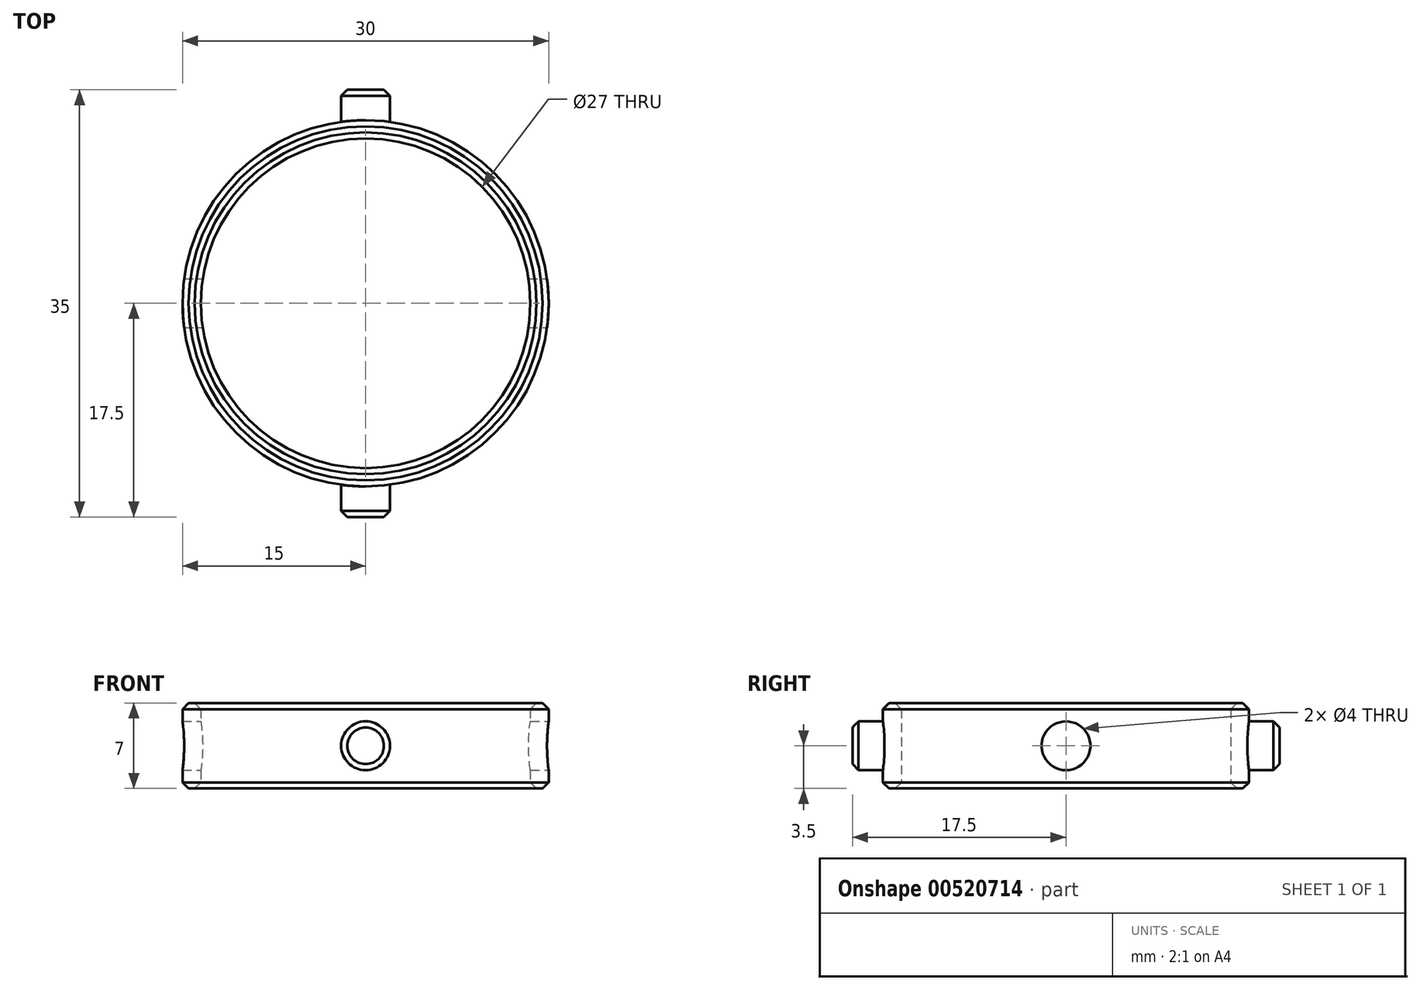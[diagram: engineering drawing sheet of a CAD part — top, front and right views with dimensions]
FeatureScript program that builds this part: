
annotation { "Feature Type Name" : "Feature", "Feature Type Description" : "" }
export const myFeature = defineFeature(function(context is Context, id is Id, definition is map)
    precondition{}
    {
        {
            var Q0;
            Q0=qCreatedBy(makeId("Top.planeOp"),FACE);
            var sketch = newSketch(context, id + "F0", { "sketchPlane" : qUnion([Q0])});
            skCircle(sketch, "E0", {"center": v(0, 0) * mm, "radius": 15 * mm});
            skCircle(sketch, "E1", {"center": v(0, 0) * mm, "radius": 13.5 * mm});
            skSolve(sketch);
        }
        {
            var Q0;
            Q0=makeQuery(id+"F0.imprint","IMPRINT",FACE,{"disambiguationData":[TD([[makeQuery(id+"F0.imprint","IMPRINT",EDGE,{"derivedFrom":sQuery(id+"F0.wireOp",EDGE,"E0")}),1.0]])]});
            extrude(context, id + "F1", {"entities" : qUnion([Q0]), "depth" : 7 * mm});
        }
        {
            var Q0;
            Q0=qCreatedBy(makeId("Right.planeOp"),FACE);
            var sketch = newSketch(context, id + "F2", { "sketchPlane" : qUnion([Q0])});
            skCircle(sketch, "E2", {"center": v(0, 3.5) * mm, "radius": 2 * mm});
            skLineSegment(sketch, "E3", {"start": v(0, 0) * mm, "end": v(0, 3.5) * mm, "construction": true});
            skLineSegment(sketch, "E4", {"start": v(0, 3.5) * mm, "end": v(0, 7) * mm, "construction": true});
            skSolve(sketch);
        }
        {
            var Q0;
            Q0=makeQuery(id+"F2.imprint","IMPRINT",FACE,{"disambiguationData":[TD([[makeQuery(id+"F2.imprint","IMPRINT",EDGE,{"derivedFrom":sQuery(id+"F2.wireOp",EDGE,"E2")}),1.0]])]});
            extrude(context, id + "F3", {"entities" : qUnion([Q0]), "operationType" : NewBodyOperationType.REMOVE, "endBound" : BoundingType.SYMMETRIC, "oppositeDirection" : true, "depth" : 40 * mm});
        }
        {
            var Q0;
            Q0=makeQuery(id+"F1.opExtrude","CAP_EDGE",EDGE,{"disambiguationData":[OSD([sQuery(id+"F0.wireOp",EDGE,"E0")])],"isStart":false});
            var Q1;
            Q1=makeQuery(id+"F1.opExtrude","CAP_EDGE",EDGE,{"disambiguationData":[OSD([sQuery(id+"F0.wireOp",EDGE,"E1")])],"isStart":false});
            var Q2;
            Q2=makeQuery(id+"F1.opExtrude","CAP_EDGE",EDGE,{"disambiguationData":[OSD([sQuery(id+"F0.wireOp",EDGE,"E0")])],"isStart":true});
            var Q3;
            Q3=makeQuery(id+"F1.opExtrude","CAP_EDGE",EDGE,{"disambiguationData":[OSD([sQuery(id+"F0.wireOp",EDGE,"E1")])],"isStart":true});
            chamfer(context, id + "F4", {"entities" : qUnion([Q0, Q1, Q2, Q3]), "width" : .5 * mm, "tangentPropagation" : true});
        }
        {
            var Q0;
            Q0=qCreatedBy(makeId("Front.planeOp"),FACE);
            cPlane(context, id + "F5", {"entities" : qUnion([Q0]), "cplaneType" : CPlaneType.OFFSET, "offset" : (27 / 2) * mm, "oppositeDirection" : true, "width" : 150 * mm, "height" : 150 * mm});
        }
        {
            var Q0;
            Q0=qCreatedBy(id+"F5.planeOp",FACE);
            var sketch = newSketch(context, id + "F6", { "sketchPlane" : qUnion([Q0])});
            skCircle(sketch, "E5", {"center": v(0, 3.5) * mm, "radius": 2 * mm});
            skLineSegment(sketch, "E6", {"start": v(0, 0) * mm, "end": v(0, 3.5) * mm, "construction": true});
            skLineSegment(sketch, "E7", {"start": v(0, 3.5) * mm, "end": v(0, 7) * mm, "construction": true});
            skSolve(sketch);
        }
        {
            var Q0;
            Q0=qSketchRegion(id+"F6",true);
            extrude(context, id + "F7", {"entities" : qUnion([Q0]), "operationType" : NewBodyOperationType.ADD, "oppositeDirection" : true, "depth" : 4 * mm});
        }
        {
            var Q0;
            Q0=makeQuery(id+"F1.opExtrude","SWEPT_BODY",BODY,{"disambiguationData":[OSD([sQuery(id+"F0.wireOp",EDGE,"E0"),sQuery(id+"F0.wireOp",EDGE,"E1")])]});
            var Q1;
            Q1=qCreatedBy(makeId("Front.planeOp"),FACE);
            mirror(context, id + "F8", {"operationType" : NewBodyOperationType.ADD, "entities" : qUnion([Q0]), "mirrorPlane" : qUnion([Q1])});
        }
        {
            var Q0;
            Q0=makeQuery(id+"F7.opExtrude","CAP_EDGE",EDGE,{"disambiguationData":[OSD([sQuery(id+"F6.wireOp",EDGE,"E5")])],"isStart":false});
            var Q1;
            Q1=makeQuery(id+"F8.opPattern","COPY",EDGE,{"derivedFrom":makeQuery(id+"F7.opExtrude","CAP_EDGE",EDGE,{"disambiguationData":[OSD([sQuery(id+"F6.wireOp",EDGE,"E5")])],"isStart":false}),"instanceName":"1"});
            chamfer(context, id + "F9", {"entities" : qUnion([Q0, Q1]), "width" : .5 * mm, "tangentPropagation" : true});
        }
    });
